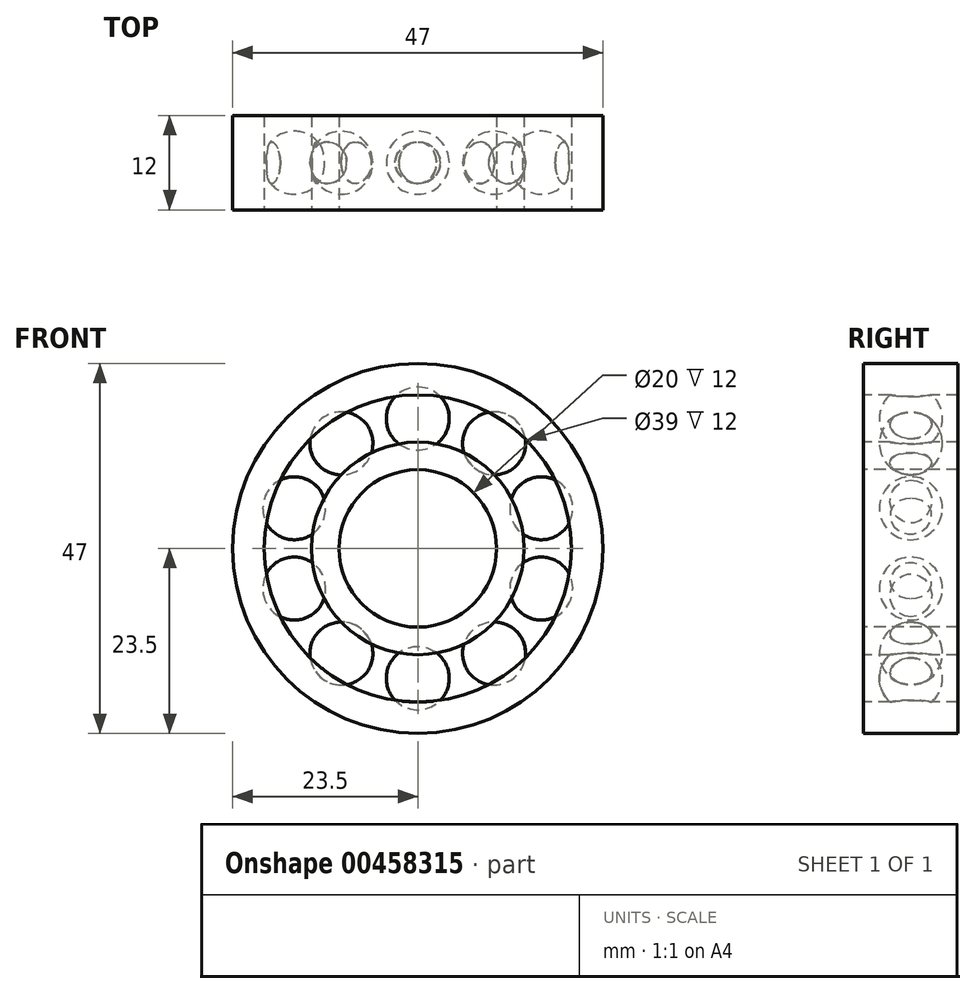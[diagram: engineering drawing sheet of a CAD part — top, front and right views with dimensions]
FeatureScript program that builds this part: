
annotation { "Feature Type Name" : "Feature", "Feature Type Description" : "" }
export const myFeature = defineFeature(function(context is Context, id is Id, definition is map)
    precondition{}
    {
        {
            var Q0;
            Q0=qCreatedBy(makeId("Front.planeOp"),FACE);
            var sketch = newSketch(context, id + "F0", { "sketchPlane" : qUnion([Q0])});
            skCircle(sketch, "E0", {"center": v(0, 0) * mm, "radius": 10 * mm});
            skCircle(sketch, "E1", {"center": v(0, 0) * mm, "radius": 13.5 * mm});
            skCircle(sketch, "E2", {"center": v(0, 0) * mm, "radius": 19.5 * mm});
            skCircle(sketch, "E3", {"center": v(0, 0) * mm, "radius": 23.5 * mm});
            skSolve(sketch);
        }
        {
            var Q0;
            Q0 = qSketchRegion(id + "F0", true);
            var Q1;
            Q1=makeQuery(id+"F0.imprint","IMPRINT",FACE,{"disambiguationData":[TD([[makeQuery(id+"F0.imprint","IMPRINT",EDGE,{"derivedFrom":sQuery(id+"F0.wireOp",EDGE,"E0")}),-1.0]])]});
            extrude(context, id + "F1", {"entities" : qUnion([Q0, Q1]), "oppositeDirection" : true, "depth" : 12 * mm});
        }
        {
            var Q0;
            Q0=qCreatedBy(makeId("Front.planeOp"),FACE);
            cPlane(context, id + "F2", {"entities" : qUnion([Q0]), "cplaneType" : CPlaneType.OFFSET, "offset" : 6 * mm, "oppositeDirection" : true, "width" : 150 * mm, "height" : 150 * mm});
        }
        {
            var Q0;
            Q0=qCreatedBy(id+"F2.planeOp",FACE);
            var sketch = newSketch(context, id + "F3", { "sketchPlane" : qUnion([Q0])});
            skArc(sketch, "E4", {"start": v(0, 12.5) * mm, "mid": v(4, 16.5) * mm, "end": v(0, 20.5) * mm});
            skLineSegment(sketch, "E5", {"start": v(0, 12.5) * mm, "end": v(0, 20.5) * mm});
            skLineSegment(sketch, "E6", {"start": v(0, 9.1) * mm, "end": v(0, 23.25) * mm, "construction": true});
            skSolve(sketch);
        }
        {
            var Q0;
            Q0=makeQuery(id+"F3.imprint","IMPRINT",FACE,{"disambiguationData":[TD([[makeQuery(id+"F3.imprint","IMPRINT",EDGE,{"derivedFrom":sQuery(id+"F3.wireOp",EDGE,"E4")}),1.0]])]});
            var Q1;
            Q1=sQuery(id+"F3.wireOp",EDGE,"E6");
            revolve(context, id + "F4", {"entities" : qUnion([Q0]), "axis" : qUnion([Q1]), "revolveType" : RevolveType.FULL});
        }
        {
            var Q0;
            Q0=qCreatedBy(makeId("Right.planeOp"),FACE);
            var sketch = newSketch(context, id + "F5", { "sketchPlane" : qUnion([Q0])});
            skLineSegment(sketch, "E7", {"start": v(0, 0) * mm, "end": v(27.28, 0) * mm, "construction": true});
            skSolve(sketch);
        }
        {
            var Q0;
            Q0=makeQuery(id+"F4.opRevolve","SWEPT_BODY",BODY,{"disambiguationData":[OSD([sQuery(id+"F3.wireOp",EDGE,"E4"),sQuery(id+"F3.wireOp",EDGE,"E5")])]});
            var Q1;
            Q1=sQuery(id+"F5.wireOp",EDGE,"E7");
            circularPattern(context, id + "F6", {"operationType" : NewBodyOperationType.ADD, "entities" : qUnion([Q0]), "axis" : qUnion([Q1]), "angle" : 360 * degree, "instanceCount" : 10, "equalSpace" : true});
        }
    });
